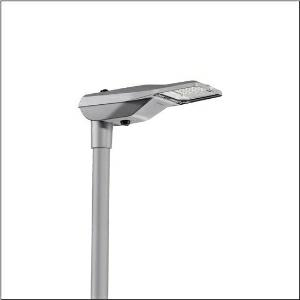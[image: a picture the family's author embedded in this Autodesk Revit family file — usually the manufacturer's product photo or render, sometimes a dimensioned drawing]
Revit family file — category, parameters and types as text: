
# Revit family: streetlight_sl_21_iq_micro___p0_8ab_5xe1r31y08cb_b23c
name_source: partatom
category: Lighting Fixtures
units: mm (PartAtom-declared; Revit-internal decimal feet)

## family parameters
Cut with Voids When Loaded = No
Host = Face
Light Source = No
Part Type = Normal
Room Calculation Point = No
Round Connector Dimension = Use Diameter
Shared = No

## types (1)
- --- (1 x LED, 2570 lm, 19.1 W, 3000K)
    Apparent Load = 19 VA
    CIE Flux Codes = 36 71 98 100 100
    Color Rendering = 70
    Color Temperature = 3000K
    Default Elevation = 1800 mm
    Description = Streetlight SL 21 iQ micro, mast luminaire, primary light control with lens, of PMMA, primary optical cover: cover, of toughened safety glass, transparent, light distribution: P0.8aB, light emission: direct distribution, primary light characteristic: asymmetric, installation type: post-top, side-entry, LED, High Power LED, rated luminous flux: 2.570lm, luminous efficacy: 135lm/W, light colour: 730, colour temperature: 3000K, control gear: iQ-Street Remote, D4i with power reduction, control: pre-setting: logarithmic dimming characteristic, Street-Remote, Auto-Match, Temp-Guard, Lumen-Switch, Night-Set, Smart-Wire, Light-Fading, Desk-Remote (wireless, voltage-free reading and setting of iQ features in the workshop via application-optimized NFC function/RFID function), optimised constant luminous flux control (CLO 2.0), mains connection: 220..240V, AC, 50/60Hz, start of lifetime: 19W, end of service life: 20W, reduction: 9W, luminaire housing, of diecast aluminium, powder-coated, Siteco® metallic grey (DB 702S), corrosivity category C5 mid according to DIN EN ISO 12944, please order mast flange separately, inclination adjustable: 0°, 5°, 10°, 15°, sealing non-destructively replaceable, multi-level sealing system, length: 528mm, width: 235mm, height: 110mm, mast flange for spigot size: 42mm (side-entry): 5XC10008XM4, 60/48mm (side-entry/post-top): 5XC10108XM2, 76/60mm (side-entry/post-top): 5XC10108XM1, mounting height: 4..8m, Smart Interface below and above, protection rating (complete): IP66, insulation class (complete): insulation class II (safety insulation), certification: CE, ENEC, ENEC+, VDE, impact resistance: IK10, permissible operating ambient temperature for outdoor applications: -40..+50°C, standard-compliant lighting for roads and squares, packaging unit: 1 piece

Light Distribution: P0.8aB
    Height = 110 mm
    Lamp = 1 x LED
    Lamp Light Flux = 2570 lm
    Lamp Power = 19.1 W
    Lamp count = 1
    Length = 528 mm
    Luminous efficacy = 135 lm/W
    Manufacturer = Siteco
    ModVariant = No
    Model = 5XE1R31Y08CB
    Number of Poles = 1
    OnlyDefault = Yes
    Power Factor = 1
    Product Name = Streetlight SL 21 iQ micro | P0.8aB
    Product group = mast luminaire | pylon top
    ProductGroupID = 6100
    Protection Class = Protection class II
    Protection Degree = IP 66
    RLX_Detail_Level = 1
    RLX_Emergency_Light_Flux = 0 lm
    RLX_Emergency_Type = 0
    RLX_Emergency_Type_DB = No
    RlxData = <blob elided: 98433 chars, md5=4e2df4bd>
    Socket = socket
    Standby Power = 0 W
    System Light Flux = 2570 lm
    System Power = 19 W
    Type Comments = factory setting: luminous flux: 100 % | dim-lin: 254 | 387 mA
    Type Image = l_1007239.jpg
    URL = http://relux.com
    VarID = @adj_075582
    Voltage = 0 V
    Weight = 0.00 kg
    Width = 235 mm

## geometry (parser evidence)
native form markers: Blend x4, Sweep x10
no freeform markers — native parametric forms only
